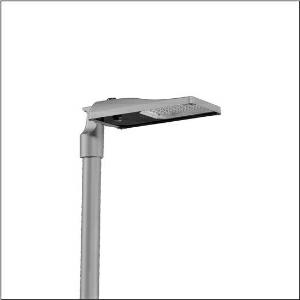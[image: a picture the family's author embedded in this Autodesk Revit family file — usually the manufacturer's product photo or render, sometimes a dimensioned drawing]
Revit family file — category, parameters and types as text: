
# Revit family: streetlight_sl_31_mini___p0_8a_5xh6u31t08ga_f82c
name_source: partatom
category: Lighting Fixtures
units: mm (PartAtom-declared; Revit-internal decimal feet)

## family parameters
Cut with Voids When Loaded = No
Host = Face
Light Source = No
Part Type = Normal
Room Calculation Point = No
Round Connector Dimension = Use Diameter
Shared = No

## types (1)
- --- (1 x LED, 5930 lm, 39.3 W, 3000K)
    Apparent Load = 39 VA
    CIE Flux Codes = 33 69 96 100 100
    Color Rendering = 70
    Color Temperature = 3000K
    Default Elevation = 1800 mm
    Description = Streetlight SL 31 mini D4i, Desk-Remote mast luminaire for post-top, side-entry; light control with lens of PMMA; light distribution: P0.8a, direct asymmetric distribution, for standard-compliant lighting for roads and squares; LED: luminous flux: 5.930lm, light colour: 730, colour temperature: 3000K; luminous efficacy: 150,9lm/W; control: pre-setting: logarithmic dimming characteristic, flexible luminous flux parameterisation, time-dependent luminous flux control, constant luminous flux control, power reduction, intelligent temperature release in ECG and LED module, overheat protection; luminaire housing, of diecast aluminium, SITECO metallic grey (DB 702S), corrosivity category C5 high according to DIN EN ISO 12944; cover of toughened safety glass, transparent, opened without tools; mast flange of diecast aluminium, SITECO metallic grey (DB 702S), spigot size: 76/60mm, mast flange included unmounted; cable length: 6,5m, connection cable pre-assembled; mains connection: 220..240V, AC, 50/60Hz; power consumption (at start of service life): 39,3W / (at end of service life): 40,7W / (with reduced operation 50%): 18,1W; protection rating (complete): IP66; insulation class (complete): insulation class II (safety insulation); impact resistance: IK09; certification: CE, ENEC, ENEC+, VDE, UKCA, ZD4i; permissible operating ambient temperature for outdoor applications: -40..+50°C; packaging unit: 1 piece

Light Distribution: P0.8a
    Height = 76 mm
    Lamp = 1 x LED
    Lamp Light Flux = 5930 lm
    Lamp Power = 39.3 W
    Lamp count = 1
    Length = 547 mm
    Luminous efficacy = 151 lm/W
    Manufacturer = Siteco
    ModVariant = No
    Model = 5XH6U31T08GA
    Number of Poles = 1
    OnlyDefault = Yes
    Power Factor = 1
    Product Name = Streetlight SL 31 mini | P0.8a
    Product group = mast luminaire | pylon top
    ProductGroupID = 6100
    Protection Class = Protection class II
    Protection Degree = IP 66
    RLX_Detail_Level = 1
    RLX_Emergency_Light_Flux = 0 lm
    RLX_Emergency_Type = 0
    RLX_Emergency_Type_DB = No
    RlxData = <blob elided: 39673 chars, md5=b5da751e>
    Socket = socket
    Standby Power = 0 W
    System Light Flux = 5930 lm
    System Power = 39 W
    Type Comments = factory setting: luminous flux: 100 % | dim-lin: 254 | 798 mA
    Type Image = l_1300332.jpg
    URL = http://relux.com
    VarID = @adj_065315
    Voltage = 0 V
    Weight = 0.00 kg
    Width = 265 mm

## geometry (parser evidence)
native form markers: Blend x4, Sweep x11
no freeform markers — native parametric forms only
